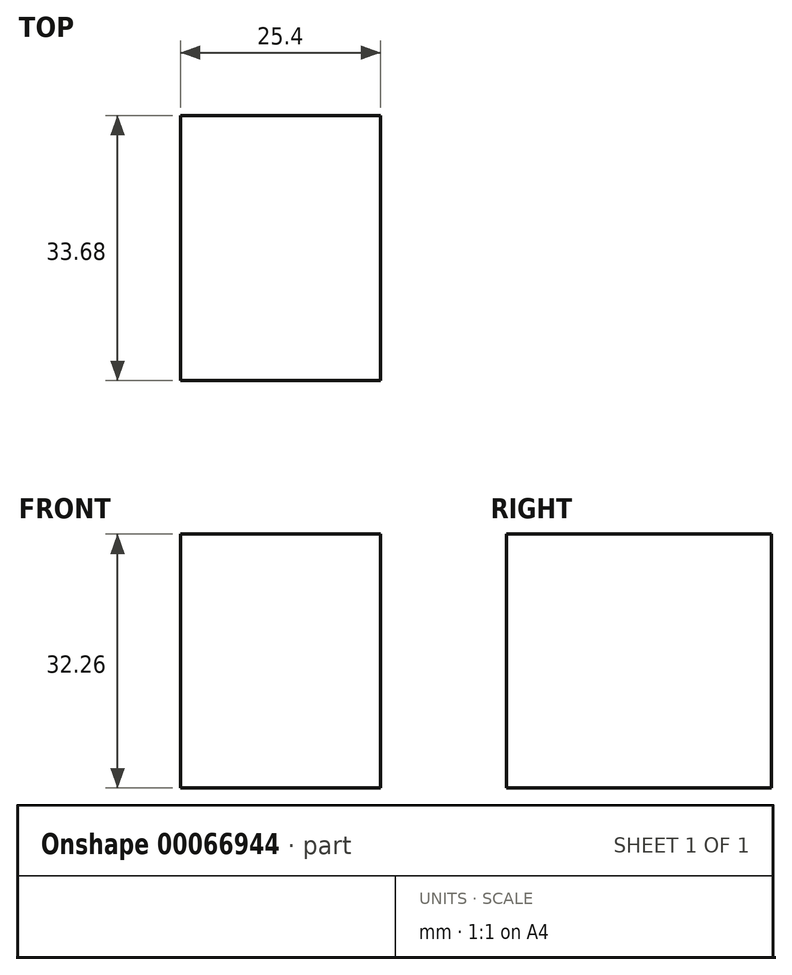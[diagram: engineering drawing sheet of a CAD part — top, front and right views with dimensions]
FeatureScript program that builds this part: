
annotation { "Feature Type Name" : "Feature", "Feature Type Description" : "" }
export const myFeature = defineFeature(function(context is Context, id is Id, definition is map)
    precondition{}
    {
        {
            var Q0;
            Q0=qCreatedBy(makeId("Right.planeOp"),FACE);
            var sketch = newSketch(context, id + "F0", { "sketchPlane" : qUnion([Q0])});
            skLineSegment(sketch, "E0.bottom", {"start": v(-65.5, 46.02) * mm, "end": v(-31.83, 46.02) * mm});
            skLineSegment(sketch, "E0.top", {"start": v(-65.5, 13.76) * mm, "end": v(-31.83, 13.76) * mm});
            skLineSegment(sketch, "E0.left", {"start": v(-65.5, 46.02) * mm, "end": v(-65.5, 13.76) * mm});
            skLineSegment(sketch, "E0.right", {"start": v(-31.83, 46.02) * mm, "end": v(-31.83, 13.76) * mm});
            skSolve(sketch);
        }
        {
            var Q0;
            Q0=makeQuery(id+"F0.imprint","IMPRINT",FACE,{"disambiguationData":[TD([[makeQuery(id+"F0.imprint","IMPRINT",EDGE,{"derivedFrom":sQuery(id+"F0.wireOp",EDGE,"E0.bottom")}),-1.0]])]});
            extrude(context, id + "F1", {"entities" : qUnion([Q0]), "depth" : 25.4 * mm});
        }
    });
